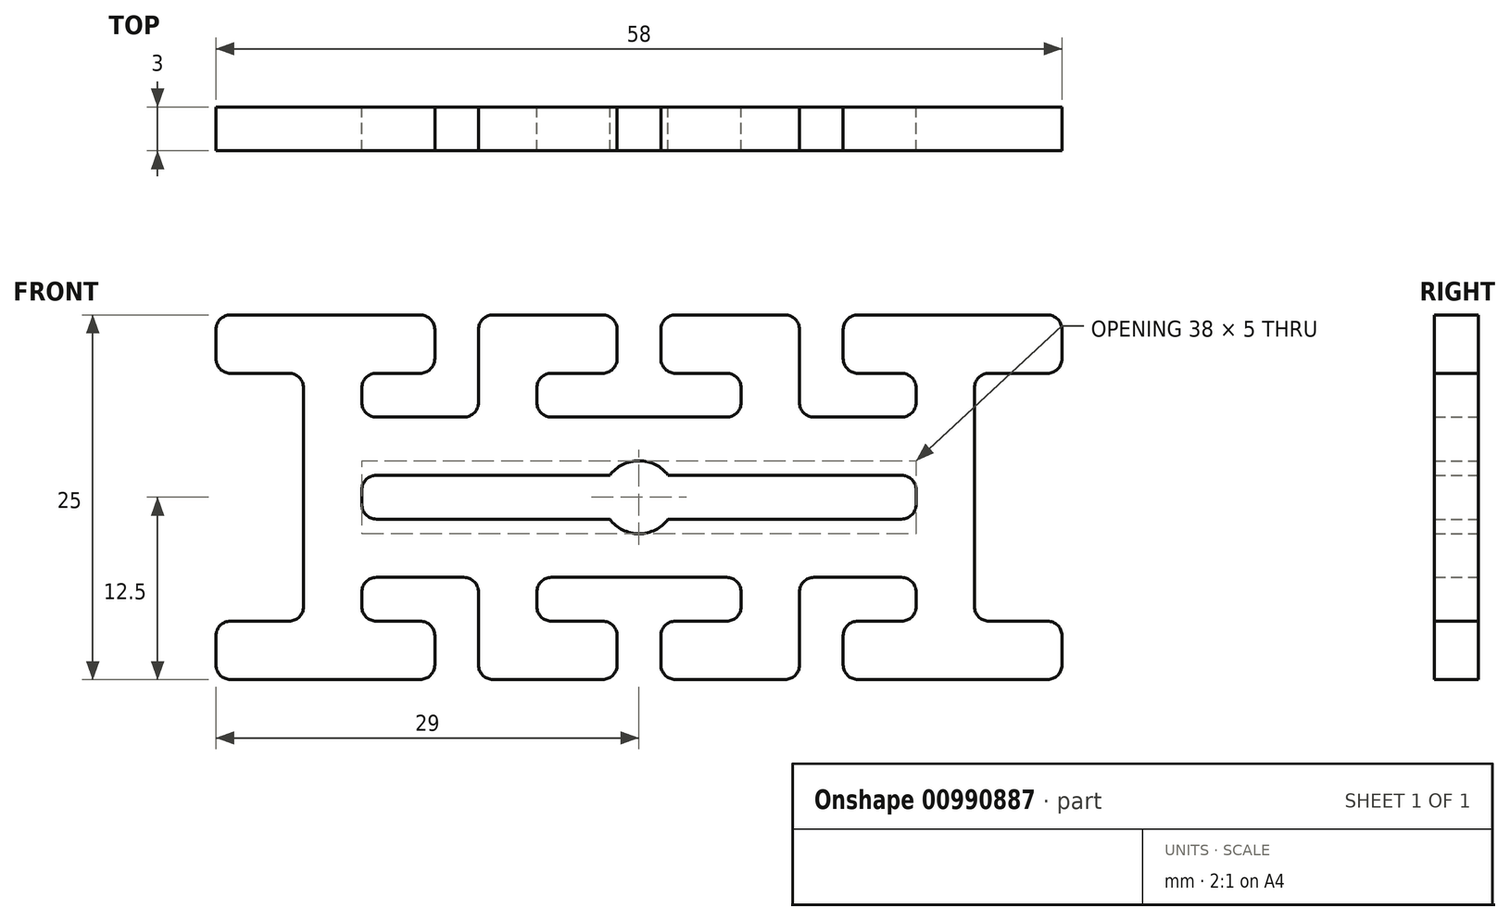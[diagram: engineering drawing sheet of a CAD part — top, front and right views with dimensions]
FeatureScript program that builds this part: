
annotation { "Feature Type Name" : "Feature", "Feature Type Description" : "" }
export const myFeature = defineFeature(function(context is Context, id is Id, definition is map)
    precondition{}
    {
        {
            var Q0;
            Q0=qCreatedBy(makeId("Front.planeOp"),FACE);
            var sketch = newSketch(context, id + "F0", { "sketchPlane" : qUnion([Q0])});
            skLineSegment(sketch, "E0.top", {"start": v(2.5, -12.5) * mm, "end": v(10, -12.5) * mm});
            skLineSegment(sketch, "E1.bottom", {"start": v(28, -8.5) * mm, "end": v(24, -8.5) * mm});
            skLineSegment(sketch, "E1.right", {"start": v(23, -7.5) * mm, "end": v(23, 0) * mm});
            skLineSegment(sketch, "E2.right", {"start": v(1.5, -11.5) * mm, "end": v(1.5, -9.5) * mm});
            skLineSegment(sketch, "E3.bottom", {"start": v(2.5, -8.5) * mm, "end": v(6, -8.5) * mm});
            skLineSegment(sketch, "E3.top", {"start": v(0, -5.5) * mm, "end": v(6, -5.5) * mm});
            skLineSegment(sketch, "E3.right", {"start": v(7, -7.5) * mm, "end": v(7, -6.5) * mm});
            skLineSegment(sketch, "E4.left", {"start": v(11, -11.5) * mm, "end": v(11, -8.5) * mm});
            skLineSegment(sketch, "E4.right", {"start": v(14, -11.5) * mm, "end": v(14, -9.5) * mm});
            skLineSegment(sketch, "E5.bottom", {"start": v(15, -8.5) * mm, "end": v(18, -8.5) * mm});
            skLineSegment(sketch, "E5.top", {"start": v(12, -5.5) * mm, "end": v(18, -5.5) * mm});
            skLineSegment(sketch, "E5.left", {"start": v(11, -8.5) * mm, "end": v(11, -6.5) * mm});
            skLineSegment(sketch, "E5.right", {"start": v(19, -7.5) * mm, "end": v(19, -6.5) * mm});
            skLineSegment(sketch, "E6.trimOffspring", {"start": v(29, -9.5) * mm, "end": v(29, -11.5) * mm});
            skPoint(sketch, "E7.visualSharp", {"position": v(23, -8.5) * mm});
            skArc(sketch, "E7.filletArc", {"start": v(23, -7.5) * mm, "mid": v(23.3, -8.2) * mm, "end": v(24, -8.5) * mm});
            skPoint(sketch, "E8.visualSharp", {"position": v(29, -8.5) * mm});
            skArc(sketch, "E8.filletArc", {"start": v(29, -9.5) * mm, "mid": v(28.7, -8.79) * mm, "end": v(28, -8.5) * mm});
            skPoint(sketch, "E9.visualSharp", {"position": v(29, -12.5) * mm});
            skArc(sketch, "E9.filletArc", {"start": v(28, -12.5) * mm, "mid": v(28.7, -12.2) * mm, "end": v(29, -11.5) * mm});
            skPoint(sketch, "E3.left.start.orphan", {"position": v(0, -8.5) * mm});
            skLineSegment(sketch, "E10.trimOffspring", {"start": v(15, -12.5) * mm, "end": v(28, -12.5) * mm});
            skPoint(sketch, "E11.visualSharp", {"position": v(7, -5.5) * mm});
            skArc(sketch, "E11.filletArc", {"start": v(7, -6.5) * mm, "mid": v(6.7, -5.79) * mm, "end": v(6, -5.5) * mm});
            skPoint(sketch, "E12.visualSharp", {"position": v(7, -8.5) * mm});
            skArc(sketch, "E12.filletArc", {"start": v(6, -8.5) * mm, "mid": v(6.7, -8.2) * mm, "end": v(7, -7.5) * mm});
            skPoint(sketch, "E13.visualSharp", {"position": v(1.5, -8.5) * mm});
            skArc(sketch, "E13.filletArc", {"start": v(2.5, -8.5) * mm, "mid": v(1.8, -8.79) * mm, "end": v(1.5, -9.5) * mm});
            skPoint(sketch, "E14.visualSharp", {"position": v(1.5, -12.5) * mm});
            skArc(sketch, "E14.filletArc", {"start": v(1.5, -11.5) * mm, "mid": v(1.8, -12.2) * mm, "end": v(2.5, -12.5) * mm});
            skPoint(sketch, "E15.visualSharp", {"position": v(11, -5.5) * mm});
            skArc(sketch, "E15.filletArc", {"start": v(12, -5.5) * mm, "mid": v(11.3, -5.79) * mm, "end": v(11, -6.5) * mm});
            skPoint(sketch, "E16.visualSharp", {"position": v(19, -5.5) * mm});
            skArc(sketch, "E16.filletArc", {"start": v(19, -6.5) * mm, "mid": v(18.7, -5.79) * mm, "end": v(18, -5.5) * mm});
            skPoint(sketch, "E17.visualSharp", {"position": v(19, -8.5) * mm});
            skArc(sketch, "E17.filletArc", {"start": v(18, -8.5) * mm, "mid": v(18.7, -8.2) * mm, "end": v(19, -7.5) * mm});
            skPoint(sketch, "E18.visualSharp", {"position": v(14, -8.5) * mm});
            skArc(sketch, "E18.filletArc", {"start": v(15, -8.5) * mm, "mid": v(14.3, -8.79) * mm, "end": v(14, -9.5) * mm});
            skPoint(sketch, "E19.visualSharp", {"position": v(14, -12.5) * mm});
            skArc(sketch, "E19.filletArc", {"start": v(14, -11.5) * mm, "mid": v(14.3, -12.2) * mm, "end": v(15, -12.5) * mm});
            skPoint(sketch, "E20.visualSharp", {"position": v(11, -12.5) * mm});
            skArc(sketch, "E20.filletArc", {"start": v(10, -12.5) * mm, "mid": v(10.7, -12.2) * mm, "end": v(11, -11.5) * mm});
            skLineSegment(sketch, "E21", {"start": v(0, -5.5) * mm, "end": v(0, -2.5) * mm});
            skLineSegment(sketch, "E22", {"start": v(19, 0) * mm, "end": v(23, 0) * mm});
            skArc(sketch, "E23", {"start": v(0, -2.5) * mm, "mid": v(1.12, -2.24) * mm, "end": v(2, -1.5) * mm});
            skLineSegment(sketch, "E24.top", {"start": v(2, -1.5) * mm, "end": v(18, -1.5) * mm});
            skLineSegment(sketch, "E24.right", {"start": v(19, 0) * mm, "end": v(19, -0.5) * mm});
            skPoint(sketch, "E25.visualSharp", {"position": v(19, -1.5) * mm});
            skArc(sketch, "E25.filletArc", {"start": v(18, -1.5) * mm, "mid": v(18.7, -1.2) * mm, "end": v(19, -0.5) * mm});
            skLineSegment(sketch, "E26.MirrorCS", {"start": v(19, 7.5) * mm, "end": v(19, 6.5) * mm});
            skLineSegment(sketch, "E27.MirrorCS", {"start": v(7, 7.5) * mm, "end": v(7, 6.5) * mm});
            skLineSegment(sketch, "E28.MirrorCS", {"start": v(19, 0) * mm, "end": v(19, 0.5) * mm});
            skArc(sketch, "E29.MirrorCS", {"start": v(1.5, 11.5) * mm, "mid": v(1.8, 12.2) * mm, "end": v(2.5, 12.5) * mm});
            skArc(sketch, "E30.MirrorCS", {"start": v(14, 11.5) * mm, "mid": v(14.3, 12.2) * mm, "end": v(15, 12.5) * mm});
            skArc(sketch, "E31.MirrorCS", {"start": v(28, 12.5) * mm, "mid": v(28.7, 12.2) * mm, "end": v(29, 11.5) * mm});
            skArc(sketch, "E32.MirrorCS", {"start": v(23, 7.5) * mm, "mid": v(23.3, 8.2) * mm, "end": v(24, 8.5) * mm});
            skArc(sketch, "E33.MirrorCS", {"start": v(18, 8.5) * mm, "mid": v(18.7, 8.2) * mm, "end": v(19, 7.5) * mm});
            skArc(sketch, "E34.MirrorCS", {"start": v(6, 8.5) * mm, "mid": v(6.7, 8.2) * mm, "end": v(7, 7.5) * mm});
            skArc(sketch, "E35.MirrorCS", {"start": v(18, 1.5) * mm, "mid": v(18.7, 1.2) * mm, "end": v(19, 0.5) * mm});
            skArc(sketch, "E36.MirrorCS", {"start": v(10, 12.5) * mm, "mid": v(10.7, 12.2) * mm, "end": v(11, 11.5) * mm});
            skArc(sketch, "E37.MirrorCS", {"start": v(12, 5.5) * mm, "mid": v(11.3, 5.79) * mm, "end": v(11, 6.5) * mm});
            skArc(sketch, "E38.MirrorCS", {"start": v(15, 8.5) * mm, "mid": v(14.3, 8.79) * mm, "end": v(14, 9.5) * mm});
            skArc(sketch, "E39.MirrorCS", {"start": v(2.5, 8.5) * mm, "mid": v(1.8, 8.79) * mm, "end": v(1.5, 9.5) * mm});
            skArc(sketch, "E40.MirrorCS", {"start": v(29, 9.5) * mm, "mid": v(28.7, 8.79) * mm, "end": v(28, 8.5) * mm});
            skArc(sketch, "E41.MirrorCS", {"start": v(19, 6.5) * mm, "mid": v(18.7, 5.79) * mm, "end": v(18, 5.5) * mm});
            skArc(sketch, "E42.MirrorCS", {"start": v(7, 6.5) * mm, "mid": v(6.7, 5.79) * mm, "end": v(6, 5.5) * mm});
            skPoint(sketch, "E43.MirrorP", {"position": v(14, 12.5) * mm});
            skLineSegment(sketch, "E44.MirrorCS", {"start": v(2.5, 8.5) * mm, "end": v(6, 8.5) * mm});
            skPoint(sketch, "E45.MirrorP", {"position": v(7, 5.5) * mm});
            skLineSegment(sketch, "E46.MirrorCS", {"start": v(11, 8.5) * mm, "end": v(11, 6.5) * mm});
            skLineSegment(sketch, "E47.MirrorCS", {"start": v(0, 5.5) * mm, "end": v(6, 5.5) * mm});
            skLineSegment(sketch, "E48.MirrorCS", {"start": v(15, 8.5) * mm, "end": v(18, 8.5) * mm});
            skLineSegment(sketch, "E49.MirrorCS", {"start": v(2, 1.5) * mm, "end": v(18, 1.5) * mm});
            skPoint(sketch, "E50.MirrorP", {"position": v(11, 5.5) * mm});
            skPoint(sketch, "E51.MirrorP", {"position": v(23, 8.5) * mm});
            skPoint(sketch, "E52.MirrorP", {"position": v(7, 8.5) * mm});
            skLineSegment(sketch, "E53.MirrorCS", {"start": v(14, 11.5) * mm, "end": v(14, 9.5) * mm});
            skLineSegment(sketch, "E54.MirrorCS", {"start": v(12, 5.5) * mm, "end": v(18, 5.5) * mm});
            skLineSegment(sketch, "E55.MirrorCS", {"start": v(15, 12.5) * mm, "end": v(28, 12.5) * mm});
            skLineSegment(sketch, "E56.MirrorCS", {"start": v(1.5, 11.5) * mm, "end": v(1.5, 9.5) * mm});
            skPoint(sketch, "E57.MirrorP", {"position": v(0, 8.5) * mm});
            skArc(sketch, "E58.MirrorCS", {"start": v(0, 2.5) * mm, "mid": v(1.12, 2.24) * mm, "end": v(2, 1.5) * mm});
            skPoint(sketch, "E59.MirrorP", {"position": v(19, 5.5) * mm});
            skPoint(sketch, "E60.MirrorP", {"position": v(11, 12.5) * mm});
            skPoint(sketch, "E61.MirrorP", {"position": v(1.5, 8.5) * mm});
            skLineSegment(sketch, "E62.MirrorCS", {"start": v(23, 7.5) * mm, "end": v(23, 0) * mm});
            skPoint(sketch, "E63.MirrorP", {"position": v(19, 1.5) * mm});
            skLineSegment(sketch, "E64.MirrorCS", {"start": v(11, 11.5) * mm, "end": v(11, 8.5) * mm});
            skPoint(sketch, "E65.MirrorP", {"position": v(1.5, 12.5) * mm});
            skPoint(sketch, "E66.MirrorP", {"position": v(29, 12.5) * mm});
            skPoint(sketch, "E67.MirrorP", {"position": v(29, 8.5) * mm});
            skLineSegment(sketch, "E68.MirrorCS", {"start": v(28, 8.5) * mm, "end": v(24, 8.5) * mm});
            skPoint(sketch, "E69.MirrorP", {"position": v(19, 8.5) * mm});
            skPoint(sketch, "E70.MirrorP", {"position": v(14, 8.5) * mm});
            skLineSegment(sketch, "E71.MirrorCS", {"start": v(0, 5.5) * mm, "end": v(0, 2.5) * mm});
            skLineSegment(sketch, "E72.MirrorCS", {"start": v(29, 9.5) * mm, "end": v(29, 11.5) * mm});
            skLineSegment(sketch, "E73.MirrorCS", {"start": v(2.5, 12.5) * mm, "end": v(10, 12.5) * mm});
            skLineSegment(sketch, "E74.MirrorCS", {"start": v(-19, 0) * mm, "end": v(-19, -0.5) * mm});
            skLineSegment(sketch, "E75.MirrorCS", {"start": v(-7, -7.5) * mm, "end": v(-7, -6.5) * mm});
            skLineSegment(sketch, "E76.MirrorCS", {"start": v(-19, -7.5) * mm, "end": v(-19, -6.5) * mm});
            skLineSegment(sketch, "E77.MirrorCS", {"start": v(-19, 7.5) * mm, "end": v(-19, 6.5) * mm});
            skLineSegment(sketch, "E78.MirrorCS", {"start": v(-19, 0) * mm, "end": v(-19, 0.5) * mm});
            skLineSegment(sketch, "E79.MirrorCS", {"start": v(-7, 7.5) * mm, "end": v(-7, 6.5) * mm});
            skArc(sketch, "E80.MirrorCS", {"start": v(-2.5, -8.5) * mm, "mid": v(-1.8, -8.79) * mm, "end": v(-1.5, -9.5) * mm});
            skArc(sketch, "E81.MirrorCS", {"start": v(-18, 1.5) * mm, "mid": v(-18.7, 1.2) * mm, "end": v(-19, 0.5) * mm});
            skArc(sketch, "E82.MirrorCS", {"start": v(-19, -6.5) * mm, "mid": v(-18.7, -5.79) * mm, "end": v(-18, -5.5) * mm});
            skArc(sketch, "E83.MirrorCS", {"start": v(-18, -1.5) * mm, "mid": v(-18.7, -1.2) * mm, "end": v(-19, -0.5) * mm});
            skArc(sketch, "E84.MirrorCS", {"start": v(-7, -6.5) * mm, "mid": v(-6.7, -5.79) * mm, "end": v(-6, -5.5) * mm});
            skArc(sketch, "E85.MirrorCS", {"start": v(-19, 6.5) * mm, "mid": v(-18.7, 5.79) * mm, "end": v(-18, 5.5) * mm});
            skArc(sketch, "E86.MirrorCS", {"start": v(-1.5, -11.5) * mm, "mid": v(-1.8, -12.2) * mm, "end": v(-2.5, -12.5) * mm});
            skArc(sketch, "E87.MirrorCS", {"start": v(-6, -8.5) * mm, "mid": v(-6.7, -8.2) * mm, "end": v(-7, -7.5) * mm});
            skArc(sketch, "E88.MirrorCS", {"start": v(-29, -9.5) * mm, "mid": v(-28.7, -8.79) * mm, "end": v(-28, -8.5) * mm});
            skArc(sketch, "E89.MirrorCS", {"start": v(-23, 7.5) * mm, "mid": v(-23.3, 8.2) * mm, "end": v(-24, 8.5) * mm});
            skArc(sketch, "E90.MirrorCS", {"start": v(-28, 12.5) * mm, "mid": v(-28.7, 12.2) * mm, "end": v(-29, 11.5) * mm});
            skArc(sketch, "E91.MirrorCS", {"start": v(-14, -11.5) * mm, "mid": v(-14.3, -12.2) * mm, "end": v(-15, -12.5) * mm});
            skArc(sketch, "E92.MirrorCS", {"start": v(-10, -12.5) * mm, "mid": v(-10.7, -12.2) * mm, "end": v(-11, -11.5) * mm});
            skArc(sketch, "E93.MirrorCS", {"start": v(-6, 8.5) * mm, "mid": v(-6.7, 8.2) * mm, "end": v(-7, 7.5) * mm});
            skArc(sketch, "E94.MirrorCS", {"start": v(-23, -7.5) * mm, "mid": v(-23.3, -8.2) * mm, "end": v(-24, -8.5) * mm});
            skArc(sketch, "E95.MirrorCS", {"start": v(-7, 6.5) * mm, "mid": v(-6.7, 5.79) * mm, "end": v(-6, 5.5) * mm});
            skArc(sketch, "E96.MirrorCS", {"start": v(-18, -8.5) * mm, "mid": v(-18.7, -8.2) * mm, "end": v(-19, -7.5) * mm});
            skArc(sketch, "E97.MirrorCS", {"start": v(-2.5, 8.5) * mm, "mid": v(-1.8, 8.79) * mm, "end": v(-1.5, 9.5) * mm});
            skArc(sketch, "E98.MirrorCS", {"start": v(-14, 11.5) * mm, "mid": v(-14.3, 12.2) * mm, "end": v(-15, 12.5) * mm});
            skArc(sketch, "E99.MirrorCS", {"start": v(-15, -8.5) * mm, "mid": v(-14.3, -8.79) * mm, "end": v(-14, -9.5) * mm});
            skArc(sketch, "E100.MirrorCS", {"start": v(-1.5, 11.5) * mm, "mid": v(-1.8, 12.2) * mm, "end": v(-2.5, 12.5) * mm});
            skArc(sketch, "E101.MirrorCS", {"start": v(-10, 12.5) * mm, "mid": v(-10.7, 12.2) * mm, "end": v(-11, 11.5) * mm});
            skArc(sketch, "E102.MirrorCS", {"start": v(-12, -5.5) * mm, "mid": v(-11.3, -5.79) * mm, "end": v(-11, -6.5) * mm});
            skArc(sketch, "E103.MirrorCS", {"start": v(-12, 5.5) * mm, "mid": v(-11.3, 5.79) * mm, "end": v(-11, 6.5) * mm});
            skArc(sketch, "E104.MirrorCS", {"start": v(-15, 8.5) * mm, "mid": v(-14.3, 8.79) * mm, "end": v(-14, 9.5) * mm});
            skArc(sketch, "E105.MirrorCS", {"start": v(-18, 8.5) * mm, "mid": v(-18.7, 8.2) * mm, "end": v(-19, 7.5) * mm});
            skArc(sketch, "E106.MirrorCS", {"start": v(-29, 9.5) * mm, "mid": v(-28.7, 8.79) * mm, "end": v(-28, 8.5) * mm});
            skArc(sketch, "E107.MirrorCS", {"start": v(-28, -12.5) * mm, "mid": v(-28.7, -12.2) * mm, "end": v(-29, -11.5) * mm});
            skLineSegment(sketch, "E108.MirrorCS", {"start": v(-11, -11.5) * mm, "end": v(-11, -8.5) * mm});
            skPoint(sketch, "E109.MirrorP", {"position": v(-14, -8.5) * mm});
            skLineSegment(sketch, "E110.MirrorCS", {"start": v(-1.5, -11.5) * mm, "end": v(-1.5, -9.5) * mm});
            skPoint(sketch, "E111.MirrorP", {"position": v(-29, -12.5) * mm});
            skLineSegment(sketch, "E112.MirrorCS", {"start": v(-15, 8.5) * mm, "end": v(-18, 8.5) * mm});
            skLineSegment(sketch, "E113.MirrorCS", {"start": v(-23, 7.5) * mm, "end": v(-23, 0) * mm});
            skLineSegment(sketch, "E114.MirrorCS", {"start": v(-15, -8.5) * mm, "end": v(-18, -8.5) * mm});
            skLineSegment(sketch, "E115.MirrorCS", {"start": v(-15, -12.5) * mm, "end": v(-28, -12.5) * mm});
            skPoint(sketch, "E116.MirrorP", {"position": v(-1.5, 8.5) * mm});
            skPoint(sketch, "E117.MirrorP", {"position": v(-23, -8.5) * mm});
            skLineSegment(sketch, "E118.MirrorCS", {"start": v(0, 5.5) * mm, "end": v(-6, 5.5) * mm});
            skPoint(sketch, "E119.MirrorP", {"position": v(-7, 8.5) * mm});
            skLineSegment(sketch, "E120.MirrorCS", {"start": v(-1.5, 11.5) * mm, "end": v(-1.5, 9.5) * mm});
            skPoint(sketch, "E121.MirrorP", {"position": v(-19, 8.5) * mm});
            skPoint(sketch, "E122.MirrorP", {"position": v(-1.5, 12.5) * mm});
            skPoint(sketch, "E123.MirrorP", {"position": v(-11, 12.5) * mm});
            skPoint(sketch, "E124.MirrorP", {"position": v(-7, 5.5) * mm});
            skLineSegment(sketch, "E125.MirrorCS", {"start": v(-2.5, -8.5) * mm, "end": v(-6, -8.5) * mm});
            skLineSegment(sketch, "E126.MirrorCS", {"start": v(-14, -11.5) * mm, "end": v(-14, -9.5) * mm});
            skPoint(sketch, "E127.MirrorP", {"position": v(-1.5, -8.5) * mm});
            skPoint(sketch, "E128.MirrorP", {"position": v(-29, 12.5) * mm});
            skPoint(sketch, "E129.MirrorP", {"position": v(-1.5, -12.5) * mm});
            skPoint(sketch, "E130.MirrorP", {"position": v(-11, -12.5) * mm});
            skLineSegment(sketch, "E131.MirrorCS", {"start": v(0, -5.5) * mm, "end": v(-6, -5.5) * mm});
            skLineSegment(sketch, "E132.MirrorCS", {"start": v(-2.5, 8.5) * mm, "end": v(-6, 8.5) * mm});
            skPoint(sketch, "E133.MirrorP", {"position": v(-19, 5.5) * mm});
            skLineSegment(sketch, "E134.MirrorCS", {"start": v(-29, 9.5) * mm, "end": v(-29, 11.5) * mm});
            skLineSegment(sketch, "E135.MirrorCS", {"start": v(-15, 12.5) * mm, "end": v(-28, 12.5) * mm});
            skLineSegment(sketch, "E136.MirrorCS", {"start": v(-11, 8.5) * mm, "end": v(-11, 6.5) * mm});
            skLineSegment(sketch, "E137.MirrorCS", {"start": v(-2.5, 12.5) * mm, "end": v(-10, 12.5) * mm});
            skLineSegment(sketch, "E138.MirrorCS", {"start": v(-23, -7.5) * mm, "end": v(-23, 0) * mm});
            skLineSegment(sketch, "E139.MirrorCS", {"start": v(-19, 0) * mm, "end": v(-23, 0) * mm});
            skPoint(sketch, "E140.MirrorP", {"position": v(-11, 5.5) * mm});
            skLineSegment(sketch, "E141.MirrorCS", {"start": v(-12, 5.5) * mm, "end": v(-18, 5.5) * mm});
            skLineSegment(sketch, "E142.MirrorCS", {"start": v(-2, -1.5) * mm, "end": v(-18, -1.5) * mm});
            skPoint(sketch, "E143.MirrorP", {"position": v(-19, 1.5) * mm});
            skPoint(sketch, "E144.MirrorP", {"position": v(-19, -8.5) * mm});
            skLineSegment(sketch, "E145.MirrorCS", {"start": v(-12, -5.5) * mm, "end": v(-18, -5.5) * mm});
            skPoint(sketch, "E146.MirrorP", {"position": v(-19, -1.5) * mm});
            skArc(sketch, "E147.MirrorCS", {"start": v(0, -2.5) * mm, "mid": v(-1.12, -2.24) * mm, "end": v(-2, -1.5) * mm});
            skPoint(sketch, "E148.MirrorP", {"position": v(-14, 8.5) * mm});
            skPoint(sketch, "E149.MirrorP", {"position": v(-11, -5.5) * mm});
            skLineSegment(sketch, "E150.MirrorCS", {"start": v(-2, 1.5) * mm, "end": v(-18, 1.5) * mm});
            skLineSegment(sketch, "E151.MirrorCS", {"start": v(-14, 11.5) * mm, "end": v(-14, 9.5) * mm});
            skPoint(sketch, "E152.MirrorP", {"position": v(-14, 12.5) * mm});
            skPoint(sketch, "E153.MirrorP", {"position": v(-23, 8.5) * mm});
            skArc(sketch, "E154.MirrorCS", {"start": v(0, 2.5) * mm, "mid": v(-1.12, 2.24) * mm, "end": v(-2, 1.5) * mm});
            skLineSegment(sketch, "E155.MirrorCS", {"start": v(-11, -8.5) * mm, "end": v(-11, -6.5) * mm});
            skLineSegment(sketch, "E156.MirrorCS", {"start": v(-2.5, -12.5) * mm, "end": v(-10, -12.5) * mm});
            skPoint(sketch, "E157.MirrorP", {"position": v(-29, -8.5) * mm});
            skLineSegment(sketch, "E158.MirrorCS", {"start": v(-11, 11.5) * mm, "end": v(-11, 8.5) * mm});
            skLineSegment(sketch, "E159.MirrorCS", {"start": v(-28, 8.5) * mm, "end": v(-24, 8.5) * mm});
            skPoint(sketch, "E160.MirrorP", {"position": v(-7, -5.5) * mm});
            skPoint(sketch, "E161.MirrorP", {"position": v(-14, -12.5) * mm});
            skLineSegment(sketch, "E162.MirrorCS", {"start": v(-28, -8.5) * mm, "end": v(-24, -8.5) * mm});
            skPoint(sketch, "E163.MirrorP", {"position": v(-19, -5.5) * mm});
            skPoint(sketch, "E164.MirrorP", {"position": v(-7, -8.5) * mm});
            skPoint(sketch, "E165.MirrorP", {"position": v(-29, 8.5) * mm});
            skLineSegment(sketch, "E166.MirrorCS", {"start": v(-29, -9.5) * mm, "end": v(-29, -11.5) * mm});
            skSolve(sketch);
        }
        {
            var Q0;
            Q0=makeQuery(id+"F0.imprint","IMPRINT",FACE,{"disambiguationData":[TD([[makeQuery(id+"F0.imprint","IMPRINT",EDGE,{"derivedFrom":sQuery(id+"F0.wireOp",EDGE,"cdSe6n1G-aW8F-UPTE-jBNw-P9OtoF522v1y.bottom")}),1.0]])]});
            var Q1;
            Q1=makeQuery(id+"F0.imprint","IMPRINT",FACE,{"disambiguationData":[TD([[makeQuery(id+"F0.imprint","IMPRINT",EDGE,{"derivedFrom":sQuery(id+"F0.wireOp",EDGE,"E77.MirrorCS")}),-1.0]])]});
            var Q2;
            Q2=makeQuery(id+"F0.imprint","IMPRINT",FACE,{"disambiguationData":[TD([[makeQuery(id+"F0.imprint","IMPRINT",EDGE,{"derivedFrom":sQuery(id+"F0.wireOp",EDGE,"E22")}),1.0]])]});
            var Q3;
            Q3=makeQuery(id+"F0.imprint","IMPRINT",FACE,{"disambiguationData":[TD([[makeQuery(id+"F0.imprint","IMPRINT",EDGE,{"derivedFrom":sQuery(id+"F0.wireOp",EDGE,"E74.MirrorCS")}),-1.0]])]});
            var Q4;
            Q4=makeQuery(id+"F0.imprint","IMPRINT",FACE,{"disambiguationData":[TD([[makeQuery(id+"F0.imprint","IMPRINT",EDGE,{"derivedFrom":sQuery(id+"F0.wireOp",EDGE,"E0.top")}),1.0]])]});
            extrude(context, id + "F1", {"entities" : qUnion([Q0, Q1, Q2, Q3, Q4]), "depth" : 3 * mm, "offsetDistance" : 25 * mm});
        }
    });
